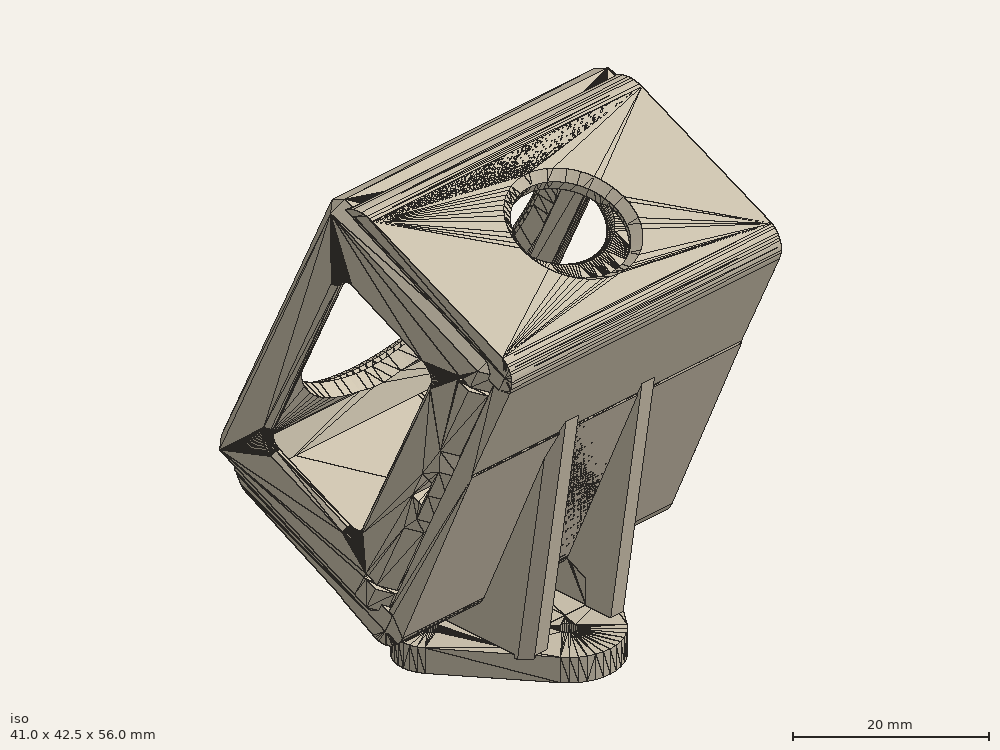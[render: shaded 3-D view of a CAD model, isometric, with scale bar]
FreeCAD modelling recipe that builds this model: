
FCSTD DOCUMENT  (FreeCAD 0.19R24267 +99 (Git))
Label: action2_25度_狗坐
License: All rights reserved
LicenseURL: http://en.wikipedia.org/wiki/All_rights_reserved
objects: Sketcher::SketchObject×8, PartDesign::Pad×5, Part::Cut×3, PartDesign::Pocket×3, PartDesign::Body×3, Part::Chamfer×3, Part::Feature×2, Part::Box×2, Part::MultiFuse×2, Mesh::Feature×1, PartDesign::Chamfer×1, Part::Cylinder×1, Part::Fuse×1
note: 43 computed .brp shape members not serialized (recipe doc carries the construction recipe); baked Part::Feature solids carry a one-line shape summary decoded from their .brp

FEATURE [Part::Feature] ______001_solid  label="狗坐"
  Placement = pos=(0,-14.1,-43.2) rot=(0,0,1;0rad)
  shape: bbox 28.18 x 20.12 x 20.46 mm, 1068 faces (baked)
FEATURE [Part::Box] Box  label="立方体"
  AttacherType = Attacher::AttachEngine3D
  Height = 14
  Length = 19
  Placement = pos=(-11.4,-17.3487,-37.085) rot=(1,0,0;0.418879rad)
  Width = 17
FEATURE [Part::Cut] Cut
  Base = -> ______001_solid
  Tool = -> Box
FEATURE [Part::Feature] DJIaction2_cassV2001_solid  label="DJIaction2_cassV2001 (Solid)"
  Placement = pos=(0,0,0.8) rot=(0,0,1;0rad)
  shape: bbox 41 x 40.9 x 54.57 mm, 13978 faces (baked)
FEATURE [Mesh::Feature] DJIaction2
  Placement = pos=(-1.3e-15,-10.5595,-12.1122) rot=(0,0.21644,-0.976296;3.14159rad)
FEATURE [Sketcher::SketchObject] Sketch
  FullyConstrained = false
  MapMode = 5
  Placement = pos=(0,0,0) rot=(0.57735,0.57735,0.57735;2.0944rad)
  Support = -> [YZ_Plane]
  sketch-geometry (20):
    g0: GeomPoint X=-11.8779 Y=-12.6655 Z=0
    g1: GeomPoint X=-0.108248 Y=-18.7716 Z=0
    g2: LineSegment StartX=-24.6153 StartY=-40.6455 StartZ=0 EndX=-24.6153 EndY=-11.9915 EndZ=0
    g3: LineSegment StartX=-24.6153 StartY=-11.9915 StartZ=0 EndX=-30.1099 EndY=-0.0706558 EndZ=0
    g4: ArcOfCircle CenterX=-27.3854 CenterY=1.18515 CenterZ=0 NormalX=0 NormalY=0 NormalZ=1 AngleXU=0 Radius=3 StartAngle=2.15583 EndAngle=3.5735
    g5: LineSegment StartX=-29.0421 StartY=3.68622 StartZ=0 EndX=-10.214 EndY=12.1607 EndZ=0
    g6: ArcOfCircle CenterX=-8.43551 CenterY=8.20941 CenterZ=0 NormalX=0 NormalY=0 NormalZ=1 AngleXU=0 Radius=4.33313 StartAngle=0.572968 EndAngle=1.99373
    g7: LineSegment StartX=-4.79441 StartY=10.5585 StartZ=0 EndX=9.54356 EndY=-19.8682 EndZ=0
    g8: ArcOfCircle CenterX=3.63879 CenterY=-22.6507 CenterZ=0 NormalX=0 NormalY=0 NormalZ=1 AngleXU=0 Radius=6.52753 StartAngle=5.53634 EndAngle=6.72355
    g9: LineSegment StartX=8.42894 StartY=-27.085 StartZ=0 EndX=-5.79484 EndY=-34.0458 EndZ=0
    g10: LineSegment StartX=-5.79484 StartY=-34.0458 StartZ=0 EndX=-5.79484 EndY=-40.6455 EndZ=0
    g11: LineSegment StartX=-5.79484 StartY=-40.6455 StartZ=0 EndX=-24.6153 EndY=-40.6455 EndZ=0
    g12: LineSegment StartX=-27.9814 StartY=0.422502 StartZ=0 EndX=-27.4298 EndY=1.92854 EndZ=0
    g13: LineSegment StartX=-27.4298 StartY=1.92854 StartZ=0 EndX=-9.86172 EndY=10.0842 EndZ=0
    g14: LineSegment StartX=-9.86172 StartY=10.0842 StartZ=0 EndX=-6.40235 EndY=8.97087 EndZ=0
    g15: LineSegment StartX=-6.40235 StartY=8.97087 StartZ=0 EndX=8.11905 EndY=-22.1001 EndZ=0
    g16: LineSegment StartX=8.11905 StartY=-22.1001 StartZ=0 EndX=7.08521 EndY=-25.9571 EndZ=0
    g17: LineSegment StartX=7.08521 StartY=-25.9571 StartZ=0 EndX=-10.3747 EndY=-34.1479 EndZ=0
    g18: LineSegment StartX=-10.3747 StartY=-34.1479 StartZ=0 EndX=-12.2539 EndY=-33.7769 EndZ=0
    g19: LineSegment StartX=-12.2539 StartY=-33.7769 StartZ=0 EndX=-27.9814 EndY=0.422502 EndZ=0
  constraints (22):
    c: Vertical(g2)
    c: Coincident(g2,g3)
    c: Tangent(g3,g4) = 1.5708
    c: Coincident(g4,g5)
    c: Tangent(g5,g6) = 1.5708
    c: Coincident(g6,g7)
    c: Tangent(g7,g8) = 1.5708
    c: Coincident(g8,g9)
    c: Coincident(g9,g10)
    c: Vertical(g10)
    c: Coincident(g10,g11)
    c: Coincident(g11,g2)
    c: Horizontal(g11)
    c: Radius(g4) = 3
    c: Coincident(g12,g13)
    c: Coincident(g13,g14)
    c: Coincident(g14,g15)
    c: Coincident(g15,g16)
    c: Coincident(g16,g17)
    c: Coincident(g17,g18)
    c: Coincident(g18,g19)
    c: Coincident(g19,g12)
FEATURE [PartDesign::Pad] Pad
  Direction = (1,1,1)
  Length = 39
  Length2 = 100
  Midplane = true
  Placement = pos=(0,0,0) rot=(0.57735,0.57735,0.57735;2.0944rad)
  Profile = -> Sketch
  Type = 0
FEATURE [Sketcher::SketchObject] Sketch002
  FullyConstrained = false
  MapMode = 5
  Placement = pos=(19.5,-4.3e-15,4.3e-15) rot=(0.57735,0.57735,0.57735;2.0944rad)
  Support = -> [Pad]
  sketch-geometry (6):
    g0: LineSegment StartX=-24.8415 StartY=-11.7709 StartZ=0 EndX=-14.5728 EndY=-35.3199 EndZ=0
    g1: ArcOfCircle CenterX=-11.8655 CenterY=-34.1393 CenterZ=0 NormalX=0 NormalY=0 NormalZ=1 AngleXU=0 Radius=2.95356 StartAngle=3.55279 EndAngle=5.24992
    g2: LineSegment StartX=-10.3532 StartY=-36.6764 StartZ=0 EndX=-4.86179 EndY=-33.6672 EndZ=0
    g3: LineSegment StartX=-4.86179 StartY=-33.6672 StartZ=0 EndX=-4.86179 EndY=-40.8624 EndZ=0
    g4: LineSegment StartX=-4.86179 StartY=-40.8624 StartZ=0 EndX=-24.8415 EndY=-40.8624 EndZ=0
    g5: LineSegment StartX=-24.8415 StartY=-40.8624 StartZ=0 EndX=-24.8415 EndY=-11.7709 EndZ=0
  constraints (9):
    c: Tangent(g0,g1) = -1.5708
    c: Coincident(g1,g2)
    c: Coincident(g2,g3)
    c: Vertical(g3)
    c: Coincident(g3,g4)
    c: Horizontal(g4)
    c: Coincident(g4,g5)
    c: Coincident(g5,g0)
    c: Vertical(g5)
FEATURE [PartDesign::Pocket] Pocket
  BaseFeature = -> Pad
  Length = 42
  Length2 = 100
  Placement = pos=(0,0,0) rot=(0.57735,0.57735,0.57735;2.0944rad)
  Profile = -> Sketch002
  Type = 0
FEATURE [Sketcher::SketchObject] Sketch003
  FullyConstrained = false
  MapMode = 5
  Placement = pos=(-6.7e-15,-6.27212,13.935) rot=(0.205419,0.205419,-0.956873;1.61487rad)
  Support = -> [Pocket]
  sketch-geometry (1):
    g0: Circle CenterX=14.8131 CenterY=0.011856 CenterZ=0 NormalX=0 NormalY=0 NormalZ=1 AngleXU=0 Radius=6.44328
FEATURE [PartDesign::Pocket] Pocket001
  BaseFeature = -> Pocket
  Length = 5
  Length2 = 100
  Placement = pos=(0,0,0) rot=(0.57735,0.57735,0.57735;2.0944rad)
  Profile = -> Sketch003
  Type = 0
FEATURE [Sketcher::SketchObject] Sketch004
  FullyConstrained = false
  MapMode = 5
  Placement = pos=(0,0.148179,0.0698264) rot=(-0.472141,-0.472141,-0.744423;1.86175rad)
  Support = -> [Pocket001]
  sketch-geometry (1):
    g0: Circle CenterX=-6.53962 CenterY=0 CenterZ=0 NormalX=0 NormalY=0 NormalZ=1 AngleXU=0 Radius=17.1695
  constraints (1):
    c: PointOnObject(g0,g-1)
FEATURE [PartDesign::Pocket] Pocket002
  BaseFeature = -> Pocket001
  Length = 5
  Length2 = 100
  Placement = pos=(0,0,0) rot=(0.57735,0.57735,0.57735;2.0944rad)
  Profile = -> Sketch004
  Type = 0
FEATURE [Sketcher::SketchObject] Sketch005
  FullyConstrained = false
  MapMode = 5
  Placement = pos=(1.17e-14,11.2586,-23.9993) rot=(0.212592,0.212592,-0.953734;1.61815rad)
  Support = -> [Pocket002]
  sketch-geometry (8):
    g0: LineSegment StartX=1.91594 StartY=19.5973 StartZ=0 EndX=3.84524 EndY=19.5973 EndZ=0
    g1: LineSegment StartX=3.84524 StartY=19.5973 StartZ=0 EndX=3.84524 EndY=18.6619 EndZ=0
    g2: LineSegment StartX=3.84524 StartY=18.6619 StartZ=0 EndX=1.91594 EndY=17.1286 EndZ=0
    g3: LineSegment StartX=1.91594 StartY=17.1286 StartZ=0 EndX=1.91594 EndY=19.5973 EndZ=0
    g4: LineSegment StartX=1.51851 StartY=-16.7716 StartZ=0 EndX=3.74988 EndY=-18.7373 EndZ=0
    g5: LineSegment StartX=3.74988 StartY=-18.7373 StartZ=0 EndX=3.74988 EndY=-19.5199 EndZ=0
    g6: LineSegment StartX=3.74988 StartY=-19.5199 StartZ=0 EndX=1.51851 EndY=-19.5093 EndZ=0
    g7: LineSegment StartX=1.51851 StartY=-19.5093 StartZ=0 EndX=1.51851 EndY=-16.7716 EndZ=0
  constraints (13):
    c: Horizontal(g0)
    c: Coincident(g0,g1)
    c: Vertical(g1)
    c: Coincident(g1,g2)
    c: Coincident(g2,g3)
    c: Coincident(g3,g0)
    c: Vertical(g3)
    c: Coincident(g4,g5)
    c: Vertical(g5)
    c: Coincident(g5,g6)
    c: Coincident(g6,g7)
    c: Coincident(g7,g4)
    c: Vertical(g7)
FEATURE [PartDesign::Pad] Pad001
  BaseFeature = -> Pocket002
  Direction = (1,1,1)
  Length = 40
  Length2 = 100
  Placement = pos=(0,0,0) rot=(0.57735,0.57735,0.57735;2.0944rad)
  Profile = -> Sketch005
  Type = 0
FEATURE [Sketcher::SketchObject] Sketch006
  FullyConstrained = false
  MapMode = 5
  Placement = pos=(-6e-16,-1.81357,-0.847593) rot=(0.644815,0.644815,-0.4104;2.36271rad)
  Support = -> [Pad001]
  sketch-geometry (20):
    g0: LineSegment StartX=-13.5866 StartY=19.5377 StartZ=0 EndX=-11.4604 EndY=19.5377 EndZ=0
    g1: LineSegment StartX=-11.4604 StartY=19.5377 StartZ=0 EndX=-11.4604 EndY=18.9559 EndZ=0
    g2: LineSegment StartX=-11.4604 StartY=18.9559 StartZ=0 EndX=-12.6134 EndY=17.9404 EndZ=0
    g3: LineSegment StartX=-12.6134 StartY=17.9404 StartZ=0 EndX=-13.5866 EndY=15.7824 EndZ=0
    g4: LineSegment StartX=-13.5866 StartY=15.7824 StartZ=0 EndX=-13.5866 EndY=19.5377 EndZ=0
    g5: LineSegment StartX=24.4522 StartY=19.5683 StartZ=0 EndX=24.4522 EndY=19.0297 EndZ=0
    g6: LineSegment StartX=24.4522 StartY=19.0297 StartZ=0 EndX=25.6188 EndY=17.9888 EndZ=0
    g7: LineSegment StartX=25.6188 StartY=17.9888 StartZ=0 EndX=26.7559 EndY=15.8493 EndZ=0
    g8: LineSegment StartX=26.7559 StartY=15.8493 StartZ=0 EndX=26.7559 EndY=19.5597 EndZ=0
    g9: LineSegment StartX=26.7559 StartY=19.5597 StartZ=0 EndX=24.4522 EndY=19.5683 EndZ=0
    g10: LineSegment StartX=-13.772 StartY=-16.0866 StartZ=0 EndX=-12.642 EndY=-18.0406 EndZ=0
    g11: LineSegment StartX=-12.642 StartY=-18.0406 StartZ=0 EndX=-11.7945 EndY=-18.8882 EndZ=0
    g12: LineSegment StartX=-11.7945 StartY=-18.8882 StartZ=0 EndX=-11.818 EndY=-19.5474 EndZ=0
    g13: LineSegment StartX=-11.818 StartY=-19.5474 StartZ=0 EndX=-13.772 EndY=-19.5474 EndZ=0
    g14: LineSegment StartX=-13.772 StartY=-19.5474 StartZ=0 EndX=-13.772 EndY=-16.0866 EndZ=0
    g15: LineSegment StartX=26.956 StartY=-14.6143 StartZ=0 EndX=25.7566 EndY=-17.9599 EndZ=0
    g16: LineSegment StartX=25.7566 StartY=-17.9599 StartZ=0 EndX=24.5099 EndY=-18.9856 EndZ=0
    g17: LineSegment StartX=24.5099 StartY=-18.9856 StartZ=0 EndX=24.5099 EndY=-19.5853 EndZ=0
    g18: LineSegment StartX=24.5099 StartY=-19.5853 StartZ=0 EndX=26.956 EndY=-19.5853 EndZ=0
    g19: LineSegment StartX=26.956 StartY=-19.5853 StartZ=0 EndX=26.956 EndY=-14.6143 EndZ=0
  constraints (30):
    c: Horizontal(g0)
    c: Coincident(g0,g1)
    c: Vertical(g1)
    c: Coincident(g1,g2)
    c: Coincident(g2,g3)
    c: Coincident(g3,g4)
    c: Coincident(g4,g0)
    c: Vertical(g4)
    c: Vertical(g5)
    c: Coincident(g5,g6)
    c: Coincident(g6,g7)
    c: Coincident(g7,g8)
    c: Vertical(g8)
    c: Coincident(g8,g9)
    c: Coincident(g9,g5)
    c: Coincident(g10,g11)
    c: Coincident(g11,g12)
    c: Coincident(g12,g13)
    c: Horizontal(g13)
    c: Coincident(g13,g14)
    c: Coincident(g14,g10)
    c: Vertical(g14)
    c: Coincident(g15,g16)
    c: Coincident(g16,g17)
    c: Vertical(g17)
    c: Coincident(g17,g18)
    c: Horizontal(g18)
    c: Coincident(g18,g19)
    c: Coincident(g19,g15)
    c: Vertical(g19)
FEATURE [PartDesign::Pad] Pad002
  BaseFeature = -> Pad001
  Direction = (1,1,1)
  Length = 24
  Length2 = 100
  Placement = pos=(0,0,0) rot=(0.57735,0.57735,0.57735;2.0944rad)
  Profile = -> Sketch006
  Type = 0
FEATURE [PartDesign::Chamfer] Chamfer
  Angle = 45
  Base = -> Pad002 [Edge112]
  BaseFeature = -> Pad002
  ChamferType = 0
  FlipDirection = false
  Placement = pos=(0,0,0) rot=(0.57735,0.57735,0.57735;2.0944rad)
  Size = 1
  Size2 = 1
  SupportTransform = false
FEATURE [PartDesign::Body] Body
  Group = -> [Sketch,Pad,Sketch002,Pocket,Sketch003,Pocket001,Sketch004,Pocket002,Sketch005,Pad001,Sketch006,Pad002,Chamfer]
  Origin = -> Origin
  Tip = -> Chamfer
FEATURE [Sketcher::SketchObject] Sketch007
  FullyConstrained = false
  MapMode = 5
  Placement = pos=(0,0,0) rot=(0.57735,0.57735,0.57735;2.0944rad)
  Support = -> [YZ_Plane001]
  sketch-geometry (5):
    g0: LineSegment StartX=-20.6202 StartY=-40.6405 StartZ=0 EndX=-25.2994 EndY=-10.194 EndZ=0
    g1: LineSegment StartX=-25.2994 StartY=-10.194 StartZ=0 EndX=-12.998 EndY=-36.3473 EndZ=0
    g2: LineSegment StartX=-12.998 StartY=-36.3473 StartZ=0 EndX=-4.99859 EndY=-33.1476 EndZ=0
    g3: LineSegment StartX=-4.99859 StartY=-33.1476 StartZ=0 EndX=-4.99859 EndY=-40.6405 EndZ=0
    g4: LineSegment StartX=-4.99859 StartY=-40.6405 StartZ=0 EndX=-20.6202 EndY=-40.6405 EndZ=0
  constraints (7):
    c: Coincident(g0,g1)
    c: Coincident(g1,g2)
    c: Coincident(g2,g3)
    c: Vertical(g3)
    c: Coincident(g3,g4)
    c: Coincident(g4,g0)
    c: Horizontal(g4)
FEATURE [PartDesign::Pad] Pad003
  Direction = (1,1,1)
  Length = 3
  Length2 = 100
  Placement = pos=(0,0,0) rot=(0.57735,0.57735,0.57735;2.0944rad)
  Profile = -> Sketch007
  Type = 0
FEATURE [PartDesign::Body] Body001
  Group = -> [Sketch007,Pad003]
  Origin = -> Origin001
  Placement = pos=(4.5,0,0) rot=(0,0,1;0rad)
  Tip = -> Pad003
FEATURE [Sketcher::SketchObject] Sketch008
  FullyConstrained = false
  MapMode = 5
  Placement = pos=(0,0,0) rot=(0.57735,0.57735,0.57735;2.0944rad)
  Support = -> [YZ_Plane002]
  sketch-geometry (5):
    g0: LineSegment StartX=-20.6202 StartY=-40.6405 StartZ=0 EndX=-25.2994 EndY=-10.194 EndZ=0
    g1: LineSegment StartX=-25.2994 StartY=-10.194 StartZ=0 EndX=-12.998 EndY=-36.3473 EndZ=0
    g2: LineSegment StartX=-12.998 StartY=-36.3473 StartZ=0 EndX=-4.99859 EndY=-33.1476 EndZ=0
    g3: LineSegment StartX=-4.99859 StartY=-33.1476 StartZ=0 EndX=-4.99859 EndY=-40.6405 EndZ=0
    g4: LineSegment StartX=-4.99859 StartY=-40.6405 StartZ=0 EndX=-20.6202 EndY=-40.6405 EndZ=0
  constraints (7):
    c: Coincident(g0,g1)
    c: Coincident(g1,g2)
    c: Coincident(g2,g3)
    c: Vertical(g3)
    c: Coincident(g3,g4)
    c: Coincident(g4,g0)
    c: Horizontal(g4)
FEATURE [PartDesign::Pad] Pad004
  Direction = (1,1,1)
  Length = 3
  Length2 = 100
  Placement = pos=(0,0,0) rot=(0.57735,0.57735,0.57735;2.0944rad)
  Profile = -> Sketch008
  Type = 0
FEATURE [PartDesign::Body] Body002
  Group = -> [Sketch008,Pad004]
  Origin = -> Origin002
  Placement = pos=(-7.7,0,0) rot=(0,0,1;0rad)
  Tip = -> Pad004
FEATURE [Part::Cylinder] Cylinder  label="圆柱体"
  Angle = 360
  AttacherType = Attacher::AttachEngine3D
  Height = 10
  Placement = pos=(14.6,-10.5408,3.91178) rot=(-1,0,0;1.13446rad)
  Radius = 1
FEATURE [Part::Cut] Cut001
  Base = -> Chamfer
  Tool = -> Cylinder
FEATURE [Part::Chamfer] Chamfer001
  Base = -> Cut001
  Edges = 1 edges r=1: [Edge116]
FEATURE [Part::Fuse] Fusion
  Base = -> Body001
  Tool = -> Body002
FEATURE [Part::MultiFuse] Fusion001
  Shapes = -> [Chamfer001,Fusion]
FEATURE [Part::MultiFuse] Fusion002
  Shapes = -> [Cut,Fusion001]
FEATURE [Part::Chamfer] Chamfer002
  Base = -> Fusion002
  Edges = 1 edges r=1.2: [Edge52]
FEATURE [Part::Chamfer] Chamfer003
  Base = -> Chamfer002
  Edges = 1 edges r=1.2: [Edge72]
FEATURE [Part::Box] Box001  label="立方体001"
  AttacherType = Attacher::AttachEngine3D
  Height = 4
  Length = 6
  Placement = pos=(2.91901,-14.5479,-40.0999) rot=(0,0,1;3.12414rad)
  Width = 3
FEATURE [Part::Cut] Cut002
  Base = -> Chamfer003
  Tool = -> Box001
